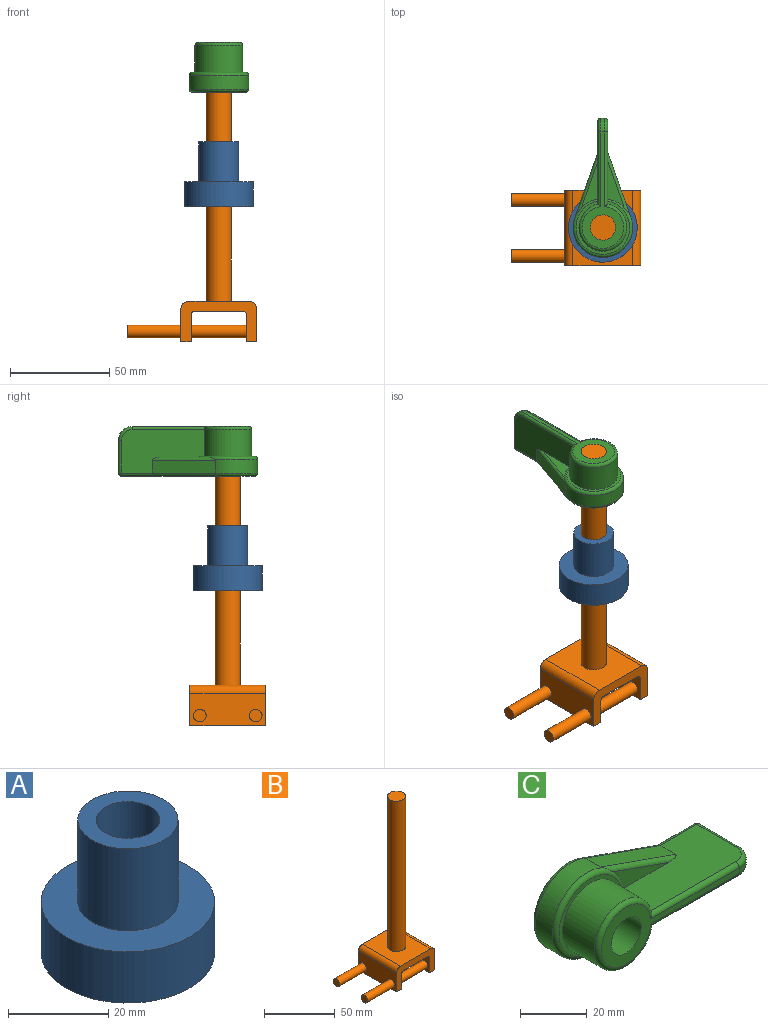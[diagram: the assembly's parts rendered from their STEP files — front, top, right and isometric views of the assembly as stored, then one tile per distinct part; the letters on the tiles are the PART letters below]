
ASSEMBLY  parts=3 mates=2
PART A: 6 faces, bbox 34.6x34.6x32.5 mm
  f0: cylinder r=17.3mm len=34.6mm, axis (0,0,-1), area 1358.7mm2, adj f1,f5
  f1: plane 34.6x34.6mm, normal (0,0,1), area 626.1mm2, adj f0,f2
  f2: cylinder r=10mm len=20mm, axis (0,0,-1), area 1256.6mm2, adj f1,f3
  f3: plane 20x20mm, normal (0,0,1), area 187.5mm2, adj f2,f4
  f4: cylinder r=6.35mm len=32.5mm, axis (0,0,-1), area 1296.7mm2, adj f3,f5
  f5: plane 34.6x34.6mm, normal (0,0,-1), area 813.6mm2, adj f0,f4
PART B: 22 faces, bbox 65.1x38.1x150.3 mm
  f0: plane 38.1x16.32mm, normal (-1,0,0), area 558.5mm2, adj f1,f8,f9,f11,f15,f18
  f1: plane 38.1x5.08mm, normal (0,0,-1), area 193.5mm2, adj f0,f2,f8,f9
  f2: plane 38.1x13.24mm, normal (1,0,0), area 441.1mm2, adj f1,f8,f9,f12,f14,f17
  f3: plane 38.1x23.94mm, normal (0,0,-1), area 912.1mm2, adj f8,f9,f12,f13
  f4: plane 38.1x13.24mm, normal (-1,0,0), area 441.1mm2, adj f5,f8,f9,f13,f14,f17
  f5: plane 38.1x5.08mm, normal (0,0,-1), area 193.5mm2, adj f4,f6,f8,f9
  f6: plane 38.1x16.32mm, normal (1,0,0), area 621.8mm2, adj f5,f8,f9,f10
  f7: plane 38.1x30.1mm, normal (0,0,1), area 1020.1mm2, adj f8,f9,f10,f11,f20
  f8: plane 38.1x20.32mm, normal (0,-1,0), area 343.2mm2, adj f0,f1,f2,f3,f4,f5,f6,f7
  f9: plane 38.1x20.32mm, normal (0,1,0), area 343.2mm2, adj f0,f1,f2,f3,f4,f5,f6,f7
  f10: cylinder r=4mm len=38.1mm, axis (0,-1,0), area 239.4mm2, adj f6,f7,f8,f9
  f11: cylinder r=4mm len=38.1mm, axis (0,1,0), area 239.4mm2, adj f0,f7,f8,f9
  f12: cylinder r=2mm len=38.1mm, axis (0,-1,0), area 119.7mm2, adj f2,f3,f8,f9
  f13: cylinder r=2mm len=38.1mm, axis (0,-1,0), area 119.7mm2, adj f3,f4,f8,f9
  f14: cylinder r=3.17mm len=27.94mm, axis (1,0,0), area 557.4mm2, adj f2,f4
  f15: cylinder r=3.17mm len=26.98mm, axis (1,0,0), area 538.2mm2, adj f0,f16
  f16: plane 6.35x6.35mm, normal (-1,0,0), area 31.7mm2, adj f15
  f17: cylinder r=3.17mm len=27.94mm, axis (1,0,0), area 557.4mm2, adj f2,f4
  f18: cylinder r=3.17mm len=26.98mm, axis (1,0,0), area 538.2mm2, adj f0,f19
  f19: plane 6.35x6.35mm, normal (-1,0,0), area 31.7mm2, adj f18
  f20: cylinder r=6.35mm len=130mm, axis (0,0,-1), area 5186.8mm2, adj f7,f21
  f21: plane 12.7x12.7mm, normal (0,0,1), area 126.7mm2, adj f20
PART C: 32 faces, bbox 71.8x25.6x32.5 mm
  f0: cylinder r=15mm len=30mm, axis (0,1,0), area 417.3mm2, adj f2,f6,f17,f28,f29,f30
  f1: plane 27x26.77mm, normal (0,-1,0), area 112.6mm2, adj f4,f9,f10,f30
  f2: plane 31.86x11.23mm, normal (0.33,0,0.94), area 220.4mm2, adj f0,f9,f13,f28
  f3: plane 23.59x8.31mm, normal (0,-1,0), area 74mm2, adj f9,f28,f30
  f4: cylinder r=12mm len=24mm, axis (0,1,0), area 949.9mm2, adj f1,f9,f10,f21
  f5: plane 67x27mm, normal (0,1,0), area 764.1mm2, adj f13,f16,f17,f20,f22,f23,f31
  f6: plane 31.86x11.23mm, normal (0.33,0,-0.94), area 220.4mm2, adj f0,f10,f20,f29
  f7: plane 23.59x8.31mm, normal (0,-1,0), area 74mm2, adj f10,f29,f30
  f8: plane 58.5x21mm, normal (0,-1,0), area 294.7mm2, adj f12,f18,f21,f24,f31
  f9: plane 41.79x22.03mm, normal (0,0,1), area 702.7mm2, adj f1,f2,f3,f4,f14,f15,f16,f18
  f10: plane 41.79x22.03mm, normal (0,0,-1), area 702.7mm2, adj f1,f4,f6,f7,f23,f24,f26,f27
  f11: plane 16.5x2mm, normal (1,0,0), area 33mm2, adj f12,f15,f22,f27
  f12: cylinder r=7mm len=7mm, axis (0,0,1), area 22mm2, adj f8,f11,f14,f26
  f13: cylinder r=1.5mm len=32.65mm, axis (-0.94,0,0.33), area 79.9mm2, adj f2,f5,f16,f17
  f14: torus R=5.5mm, axis (0,0,-1), area 23.9mm2, adj f9,f12,f15,f18
  f15: cylinder r=1.5mm len=16.5mm, axis (0,-1,0), area 38.9mm2, adj f9,f11,f14,f19
  f16: cylinder r=1.5mm len=15.85mm, axis (-1,0,0), area 37mm2, adj f5,f9,f13,f19
  f17: torus R=13.5mm, axis (0,-1,0), area 135.4mm2, adj f0,f5,f13,f20
  f18: cylinder r=1.5mm len=37.55mm, axis (-1,0,0), area 86.5mm2, adj f8,f9,f14,f21
  f19: sphere r=1.5mm, area 3.5mm2, adj f15,f16,f22
  f20: cylinder r=1.5mm len=32.65mm, axis (0.94,0,0.33), area 79.9mm2, adj f5,f6,f17,f23
  f21: torus R=10.5mm, axis (0,-1,0), area 160.3mm2, adj f4,f8,f18,f24
  f22: cylinder r=1.5mm len=2mm, axis (0,0,1), area 4.7mm2, adj f5,f11,f19,f25
  f23: cylinder r=1.5mm len=15.85mm, axis (1,0,0), area 37mm2, adj f5,f10,f20,f25
  f24: cylinder r=1.5mm len=37.55mm, axis (1,0,0), area 86.5mm2, adj f8,f10,f21,f26
  f25: sphere r=1.5mm, area 3.5mm2, adj f22,f23,f27
  f26: torus R=5.5mm, axis (0,0,-1), area 23.9mm2, adj f10,f12,f24,f27
  f27: cylinder r=1.5mm len=16.5mm, axis (0,1,0), area 38.9mm2, adj f10,f11,f25,f26
  f28: cylinder r=1.5mm len=32.36mm, axis (0.94,0,-0.33), area 70.9mm2, adj f0,f2,f3,f9,f30
  f29: cylinder r=1.5mm len=32.36mm, axis (-0.94,0,-0.33), area 70.9mm2, adj f0,f6,f7,f10,f30
  f30: torus R=13.5mm, axis (0,-1,0), area 174mm2, adj f0,f1,f3,f7,f9,f10,f28,f29
  f31: cylinder r=6.35mm len=25mm, axis (0,-1,0), area 997.5mm2, adj f5,f8
PLACE A t=(-70.59,69.5,112.67)mm fixed
PLACE B rot(axis=(0,0,1),0deg) t=(-70.59,88.55,55.01)mm
PLACE C rot(axis=(-0.58,-0.58,0.58),120deg) t=(-70.59,69.5,170.17)mm
MATE revolute A.f0 <-> B.f20  axis (0,0,-1) through (-70.59,69.5,145.17)mm
MATE fastened C.f31 <-> B.f20  axis (0,0,1) through (-70.59,69.5,195.17)mm
